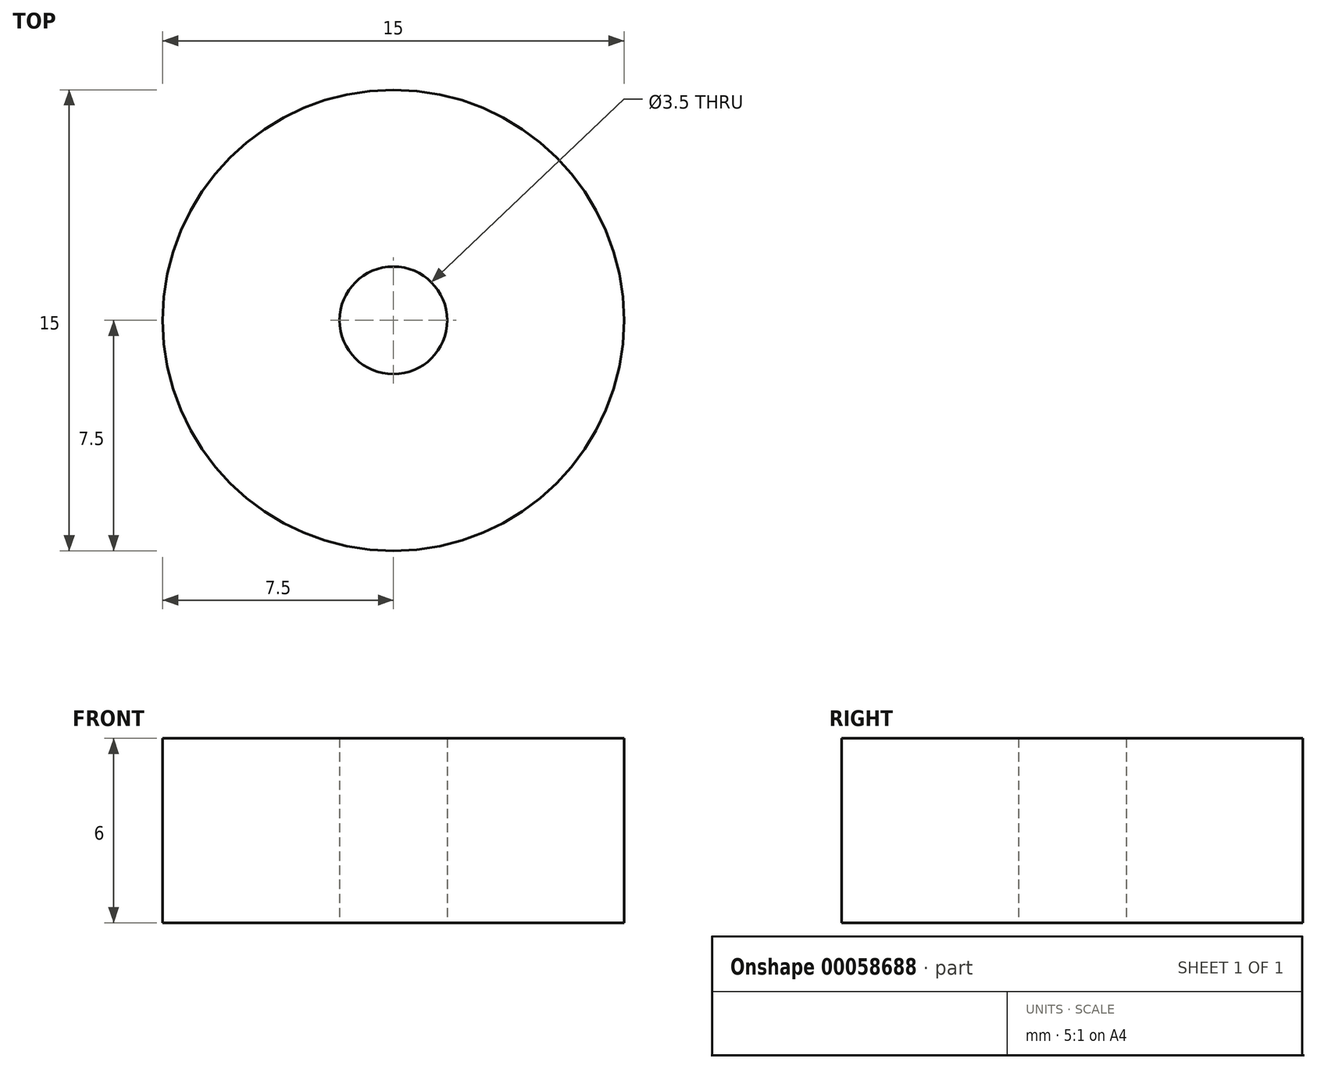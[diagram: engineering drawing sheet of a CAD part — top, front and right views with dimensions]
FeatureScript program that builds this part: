
annotation { "Feature Type Name" : "Feature", "Feature Type Description" : "" }
export const myFeature = defineFeature(function(context is Context, id is Id, definition is map)
    precondition{}
    {
        {
            var Q0;
            Q0=qCreatedBy(makeId("Top.planeOp"),FACE);
            var sketch = newSketch(context, id + "F0", { "sketchPlane" : qUnion([Q0])});
            skCircle(sketch, "E0", {"center": v(0, 0) * mm, "radius": 1.75 * mm});
            skCircle(sketch, "E1", {"center": v(0, 0) * mm, "radius": 7.5 * mm});
            skSolve(sketch);
        }
        {
            var Q0;
            Q0 = qSketchRegion(id + "F0", true);
            extrude(context, id + "F1", {"entities" : qUnion([Q0]), "depth" : 6 * mm});
        }
    });
